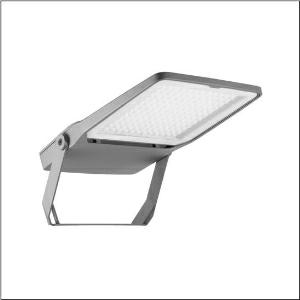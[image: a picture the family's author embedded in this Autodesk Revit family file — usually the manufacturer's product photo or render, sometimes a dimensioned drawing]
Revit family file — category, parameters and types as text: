
# Revit family: floodlight_fl_20_midi___pl61_5xa7682d1c1ac_5419
name_source: partatom
category: Lighting Fixtures
units: mm (PartAtom-declared; Revit-internal decimal feet)

## family parameters
Cut with Voids When Loaded = No
Host = Face
Light Source = No
Part Type = Normal
Room Calculation Point = No
Round Connector Dimension = Use Diameter
Shared = No

## types (1)
- --- (1 x LED 3000K / CRI = 80 (unbekannt), 14290 lm, 3000K)
    Apparent Load = 142 VA
    CIE Flux Codes = 33 65 98 100 100
    Color Rendering = 80
    Color Temperature = 3000K
    Default Elevation = 1800 mm
    Description = Floodlight FL 20 midi, floodlight, primary light control with lens, of plastic, primary optical cover: protective disc, of toughened safety glass, transparent, light distribution: PL61, light emission: direct distribution, primary light characteristic: asymmetric, installation type: surface-mounted, LED, High Power LED, rated luminous flux: 14.290lm, luminous efficacy: 101lm/W, light colour: 830, colour temperature: 3000K, control gear: ECG Plus, control: digital communication interface, time-dependent luminous flux control, flexible luminous flux parameterisation, power reduction, overheat protection, electronic power reduction, with terminal, 5-pole, max. 2.5mm², mains connection: 220..240V, AC, 50/60Hz, rated input power: 142W, LED unit, of diecast aluminium, powder-coated, Siteco® metallic grey (DB 702S), corrosivity category C5 mid according to DIN EN ISO 12944, incl. 1x M20 cable gland for cable Ø 6.5..12mm, length: 654mm, width: 450mm, height: 76mm, housing frame, of diecast aluminium, powder-coated, Siteco® metallic grey (DB 702S), mounting bracket, of steel, powder-coated, Siteco® metallic grey (DB 702S), DALI, protection rating (complete): IP66, insulation class (complete): insulation class II (safety insulation), certification: CE, ENEC, VDE, protection symbol: D, permissible operating ambient temperature: -40..+40°C, permissible operating ambient temperature for outdoor applications: -40..+50°C, standard: DIN EN 12944, packaging unit: 1 piece

Light Distribution: PL61
    Height = 76 mm
    Lamp = 1 x LED 3000K / CRI >= 80 (unbekannt)
    Lamp Light Flux = 14290 lm
    Lamp count = 1
    Length = 672 mm
    Luminous efficacy = 101 lm/W
    Manufacturer = Siteco
    ModVariant = No
    Model = 5XA7682D1C1AC
    Mounting Place = Wall
    Mounting Type = Surface mounted
    Number of Poles = 1
    OnlyDefault = Yes
    Power Factor = 1
    Product Name = Floodlight FL 20 midi | PL61
    Product group = floodlight | wall mounted
    ProductGroupID = 2001
    Protection Class = Protection class II
    Protection Degree = IP 66
    RLX_Detail_Level = 1
    RLX_Emergency_Light_Flux = 0 lm
    RLX_Emergency_Type = 0
    RLX_Emergency_Type_DB = No
    RlxData = <blob elided: 98177 chars, md5=1dbeeea7>
    Socket = socket
    Standby Power = 0 W
    System Light Flux = 14290 lm
    System Power = 142 W
    Type Comments = factory setting: luminous flux: 100 % | dim-lin: 254 | 489 mA
    Type Image = l_1005943.jpg
    URL = http://relux.com
    VarID = @adj_147389
    Voltage = 0 V
    Weight = 0.00 kg
    Width = 450 mm

## geometry (parser evidence)
native form markers: Blend x4, Sweep x11
no freeform markers — native parametric forms only
